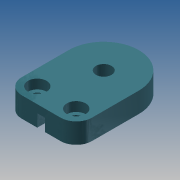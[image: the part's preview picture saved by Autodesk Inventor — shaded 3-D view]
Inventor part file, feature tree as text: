
AUTODESK INVENTOR PART (.ipt)
format: ipt  version: 2013 (Build 170138000, 138)  size: 155,136 bytes
history: native  units: mm
features: extrude x5, sketch x5, fillet x2
ambient origin geometry x8: Origin, YZ Plane, XZ Plane, XY Plane, X Axis, Y Axis, Z Axis, Center Point
bodies: Solid1 (feature_tree)
feature tree (12):
  extrude  "Extrusion1"  Depth=7.0mm
  fillet  "Fillet1"  Radius=1.5mm
  extrude  "Extrusion2"  Depth=11.25mm
  extrude  "Extrusion3"  Depth=5.0mm
  extrude  "Extrusion4"  Depth=10.0mm
  fillet  "Fillet2"  Radius=11.25mm
  extrude  "Extrusion5"  Depth=6.0mm
  sketch  "Sketch1"  dims[d0=2.5mm d3=7.0mm d4=1.5mm]
  sketch  "Sketch2"  dims[d7=6.5mm d8=0.0mm d9=11.25mm]
  sketch  "Sketch3"  dims[d10=2.5mm d11=0.0mm d13=5.0mm]
  sketch  "Sketch4"  dims[d14=3.5mm d15=10.0mm d16=11.25mm]
  sketch  "Sketch5"  dims[d17=3.5mm d18=0.0mm d19=6.0mm d21=3.0mm d22=0.0mm d23=11.25mm d24=8.0mm d25=5.0mm d26=5.0mm d28=10.0mm d29=0.0mm]
